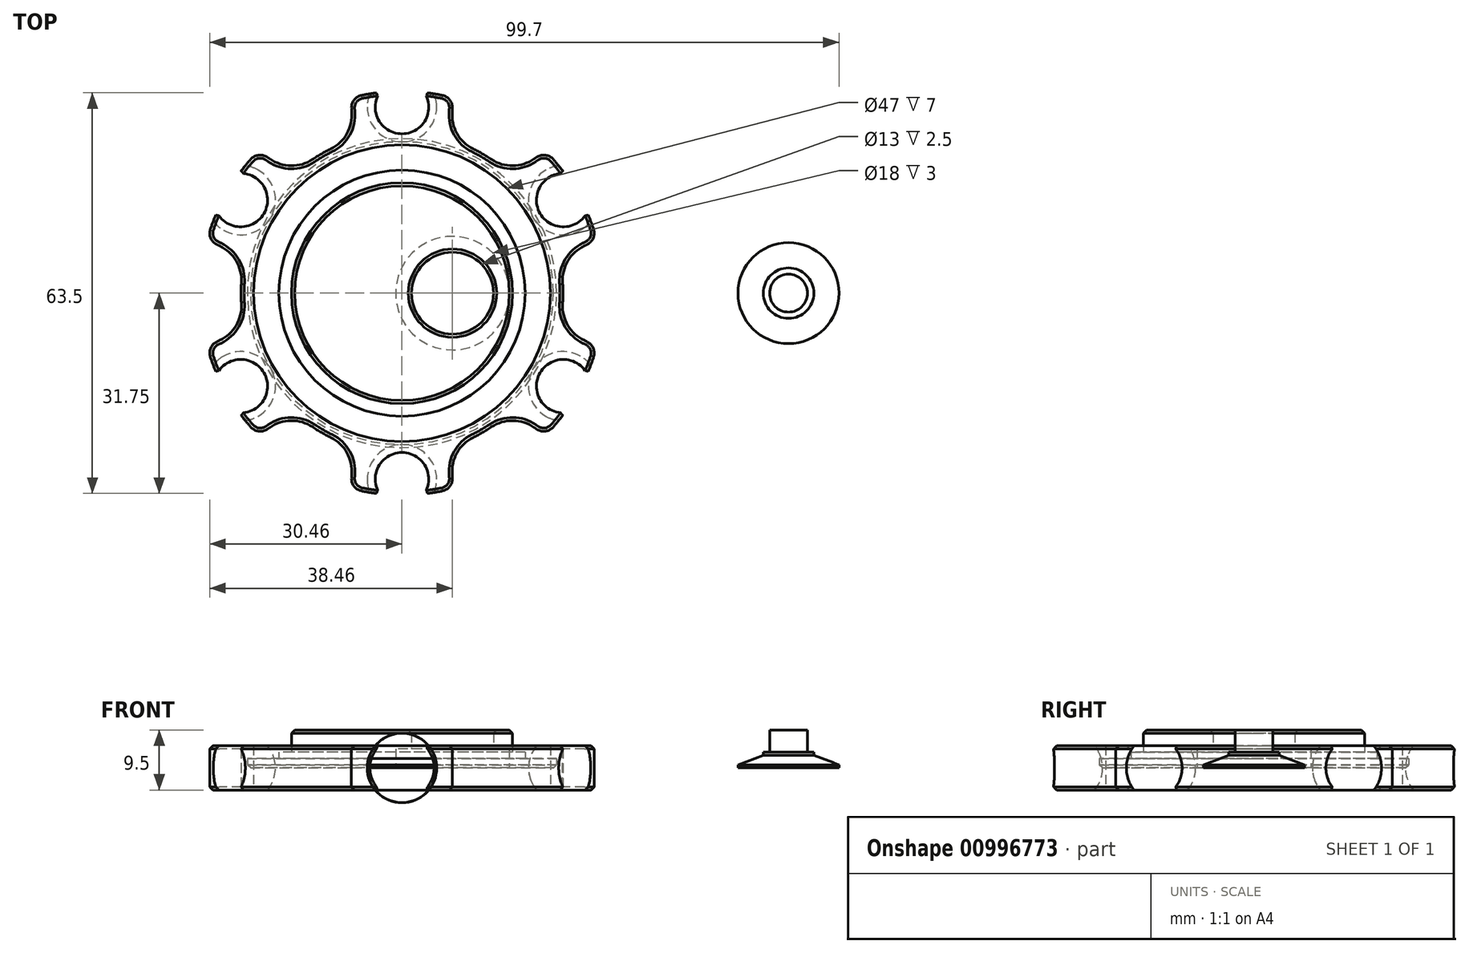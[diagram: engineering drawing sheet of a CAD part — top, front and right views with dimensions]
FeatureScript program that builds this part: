
annotation { "Feature Type Name" : "Feature", "Feature Type Description" : "" }
export const myFeature = defineFeature(function(context is Context, id is Id, definition is map)
    precondition{}
    {
        {
            var Q0;
            Q0=qCreatedBy(makeId("Top.planeOp"),FACE);
            var sketch = newSketch(context, id + "F0", { "sketchPlane" : qUnion([Q0])});
            skArc(sketch, "E0", {"start": v(-6.39, 24.69) * mm, "mid": v(0, -25.5) * mm, "end": v(6.39, 24.69) * mm});
            skArc(sketch, "E1", {"start": v(-2.55, 31.9) * mm, "mid": v(0, 26) * mm, "end": v(2.55, 31.9) * mm});
            skArc(sketch, "E2", {"start": v(7.85, 31.02) * mm, "mid": v(5.22, 31.57) * mm, "end": v(2.55, 31.9) * mm});
            skArc(sketch, "E3", {"start": v(-7.85, 31.02) * mm, "mid": v(-7.8, 27.7) * mm, "end": v(-6.39, 24.69) * mm});
            skArc(sketch, "E4.trimOffspring", {"start": v(6.39, 24.69) * mm, "mid": v(7.8, 27.7) * mm, "end": v(7.85, 31.02) * mm});
            skArc(sketch, "E5.trimOffspring", {"start": v(-2.55, 31.9) * mm, "mid": v(-5.22, 31.57) * mm, "end": v(-7.85, 31.02) * mm});
            skCircle(sketch, "E6", {"center": v(0, 0) * mm, "radius": 23.5 * mm});
            skSolve(sketch);
        }
        {
            var Q0;
            Q0=makeQuery(id+"F0.imprint","IMPRINT",FACE,{"disambiguationData":[TD([[makeQuery(id+"F0.imprint","IMPRINT",EDGE,{"derivedFrom":sQuery(id+"F0.wireOp",EDGE,"E0")}),1.0]])]});
            extrude(context, id + "F1", {"entities" : qUnion([Q0]), "depth" : 3.5 * mm, "offsetDistance" : 25 * mm, "hasSecondDirection" : true, "secondDirectionOppositeDirection" : true, "secondDirectionDepth" : 3.5 * mm});
        }
        {
            var Q0;
            Q0=makeQuery(id+"F1.opExtrude","SWEPT_EDGE",EDGE,{"disambiguationData":[OSD([sQuery(id+"F0.wireOp",EDGE,"E0"),sQuery(id+"F0.wireOp",EDGE,"E3")])]});
            var Q1;
            Q1=makeQuery(id+"F1.opExtrude","SWEPT_EDGE",EDGE,{"disambiguationData":[OSD([sQuery(id+"F0.wireOp",EDGE,"E0"),sQuery(id+"F0.wireOp",EDGE,"E4.trimOffspring")])]});
            fillet(context, id + "F2", {"entities" : qUnion([Q0, Q1]), "radius" : 6 * mm, "tangentPropagation" : true, "allowEdgeOverflow" : false});
        }
        {
            var Q0;
            Q0=makeQuery(id+"F1.opExtrude","SWEPT_EDGE",EDGE,{"disambiguationData":[OSD([sQuery(id+"F0.wireOp",EDGE,"E3"),sQuery(id+"F0.wireOp",EDGE,"E5.trimOffspring")])]});
            var Q1;
            Q1=makeQuery(id+"F1.opExtrude","SWEPT_EDGE",EDGE,{"disambiguationData":[OSD([sQuery(id+"F0.wireOp",EDGE,"E2"),sQuery(id+"F0.wireOp",EDGE,"E4.trimOffspring")])]});
            fillet(context, id + "F3", {"entities" : qUnion([Q0, Q1]), "radius" : 2 * mm, "tangentPropagation" : true, "allowEdgeOverflow" : false});
        }
        {
            var Q0;
            Q0=makeQuery(id+"F7.boolean.opBoolean","INTERSECT",EDGE,{"derivedFrom":[makeQuery(id+"F1.opExtrude","CAP_FACE",FACE,{"disambiguationData":[OSD([sQuery(id+"F0.wireOp",EDGE,"E0"),sQuery(id+"F0.wireOp",EDGE,"E1"),sQuery(id+"F0.wireOp",EDGE,"E2"),sQuery(id+"F0.wireOp",EDGE,"E3"),sQuery(id+"F0.wireOp",EDGE,"E4.trimOffspring"),sQuery(id+"F0.wireOp",EDGE,"E5.trimOffspring"),sQuery(id+"F0.wireOp",EDGE,"E6")])],"isStart":false}),makeQuery(id+"F7.opRevolve","SWEPT_FACE",FACE,{"disambiguationData":[OSD([sQuery(id+"F6.wireOp",EDGE,"E9")])]})]});
            var Q1;
            Q1=makeQuery(id+"F7.boolean.opBoolean","INTERSECT",EDGE,{"derivedFrom":[makeQuery(id+"F1.opExtrude","CAP_FACE",FACE,{"disambiguationData":[OSD([sQuery(id+"F0.wireOp",EDGE,"E0"),sQuery(id+"F0.wireOp",EDGE,"E1"),sQuery(id+"F0.wireOp",EDGE,"E2"),sQuery(id+"F0.wireOp",EDGE,"E3"),sQuery(id+"F0.wireOp",EDGE,"E4.trimOffspring"),sQuery(id+"F0.wireOp",EDGE,"E5.trimOffspring"),sQuery(id+"F0.wireOp",EDGE,"E6")])],"isStart":true}),makeQuery(id+"F7.opRevolve","SWEPT_FACE",FACE,{"disambiguationData":[OSD([sQuery(id+"F6.wireOp",EDGE,"E9")])]})]});
            var Q2;
            Q2=makeQuery(id+"F1.opExtrude","CAP_EDGE",EDGE,{"disambiguationData":[OSD([sQuery(id+"F0.wireOp",EDGE,"E5.trimOffspring")])],"isStart":true});
            var Q3;
            {var subQ0=sQuery(id+"F0.wireOp",EDGE,"E5.trimOffspring");var subQ1=sQuery(id+"F0.wireOp",EDGE,"E3");Q3=makeQuery(id+"F2.opFillet","BLEND_EDGE",EDGE,{"blendedFrom":[makeQuery(id+"F1.opExtrude","SWEPT_EDGE",EDGE,{"disambiguationData":[OSD([subQ1,subQ0])]}),makeQuery(id+"F1.opExtrude","CAP_FACE",FACE,{"disambiguationData":[OSD([sQuery(id+"F0.wireOp",EDGE,"E0"),sQuery(id+"F0.wireOp",EDGE,"E1"),sQuery(id+"F0.wireOp",EDGE,"E2"),subQ1,sQuery(id+"F0.wireOp",EDGE,"E4.trimOffspring"),subQ0,sQuery(id+"F0.wireOp",EDGE,"E6")])],"isStart":true})],"blendedInto":[makeQuery(id+"F1.opExtrude","CAP_FACE",FACE,{"disambiguationData":[OSD([sQuery(id+"F0.wireOp",EDGE,"E0"),sQuery(id+"F0.wireOp",EDGE,"E1"),sQuery(id+"F0.wireOp",EDGE,"E2"),subQ1,sQuery(id+"F0.wireOp",EDGE,"E4.trimOffspring"),subQ0,sQuery(id+"F0.wireOp",EDGE,"E6")])],"isStart":true})]});}
            var Q4;
            {var subQ0=sQuery(id+"F0.wireOp",EDGE,"E3");var subQ1=sQuery(id+"F0.wireOp",EDGE,"E0");Q4=makeQuery(id+"F2.opFillet","BLEND_EDGE",EDGE,{"blendedFrom":[makeQuery(id+"F1.opExtrude","SWEPT_EDGE",EDGE,{"disambiguationData":[OSD([subQ1,subQ0])]}),makeQuery(id+"F1.opExtrude","CAP_FACE",FACE,{"disambiguationData":[OSD([subQ1,sQuery(id+"F0.wireOp",EDGE,"E1"),sQuery(id+"F0.wireOp",EDGE,"E2"),subQ0,sQuery(id+"F0.wireOp",EDGE,"E4.trimOffspring"),sQuery(id+"F0.wireOp",EDGE,"E5.trimOffspring"),sQuery(id+"F0.wireOp",EDGE,"E6")])],"isStart":true})],"blendedInto":[makeQuery(id+"F1.opExtrude","CAP_FACE",FACE,{"disambiguationData":[OSD([subQ1,sQuery(id+"F0.wireOp",EDGE,"E1"),sQuery(id+"F0.wireOp",EDGE,"E2"),subQ0,sQuery(id+"F0.wireOp",EDGE,"E4.trimOffspring"),sQuery(id+"F0.wireOp",EDGE,"E5.trimOffspring"),sQuery(id+"F0.wireOp",EDGE,"E6")])],"isStart":true})]});}
            var Q5;
            Q5=makeQuery(id+"F1.opExtrude","CAP_EDGE",EDGE,{"disambiguationData":[OSD([sQuery(id+"F0.wireOp",EDGE,"E2")])],"isStart":false});
            var Q6;
            {var subQ0=sQuery(id+"F0.wireOp",EDGE,"E4.trimOffspring");var subQ1=sQuery(id+"F0.wireOp",EDGE,"E2");Q6=makeQuery(id+"F2.opFillet","BLEND_EDGE",EDGE,{"blendedFrom":[makeQuery(id+"F1.opExtrude","SWEPT_EDGE",EDGE,{"disambiguationData":[OSD([subQ1,subQ0])]}),makeQuery(id+"F1.opExtrude","CAP_FACE",FACE,{"disambiguationData":[OSD([sQuery(id+"F0.wireOp",EDGE,"E0"),sQuery(id+"F0.wireOp",EDGE,"E1"),subQ1,sQuery(id+"F0.wireOp",EDGE,"E3"),subQ0,sQuery(id+"F0.wireOp",EDGE,"E5.trimOffspring"),sQuery(id+"F0.wireOp",EDGE,"E6")])],"isStart":false})],"blendedInto":[makeQuery(id+"F1.opExtrude","CAP_FACE",FACE,{"disambiguationData":[OSD([sQuery(id+"F0.wireOp",EDGE,"E0"),sQuery(id+"F0.wireOp",EDGE,"E1"),subQ1,sQuery(id+"F0.wireOp",EDGE,"E3"),subQ0,sQuery(id+"F0.wireOp",EDGE,"E5.trimOffspring"),sQuery(id+"F0.wireOp",EDGE,"E6")])],"isStart":false})]});}
            var Q7;
            Q7=makeQuery(id+"F7.boolean.opBoolean","INTERSECT",EDGE,{"derivedFrom":[makeQuery(id+"F1.opExtrude","SWEPT_FACE",FACE,{"disambiguationData":[OSD([sQuery(id+"F0.wireOp",EDGE,"E5.trimOffspring")])]}),makeQuery(id+"F7.opRevolve","SWEPT_FACE",FACE,{"disambiguationData":[OSD([sQuery(id+"F6.wireOp",EDGE,"E9")])]})]});
            var Q8;
            Q8=makeQuery(id+"F7.boolean.opBoolean","INTERSECT",EDGE,{"derivedFrom":[makeQuery(id+"F1.opExtrude","SWEPT_FACE",FACE,{"disambiguationData":[OSD([sQuery(id+"F0.wireOp",EDGE,"E2")])]}),makeQuery(id+"F7.opRevolve","SWEPT_FACE",FACE,{"disambiguationData":[OSD([sQuery(id+"F6.wireOp",EDGE,"E9")])]})]});
            chamfer(context, id + "F4", {"entities" : qUnion([Q0, Q1, Q2, Q3, Q4, Q5, Q6, Q7, Q8]), "width" : 0.5 * mm, "tangentPropagation" : true});
        }
        {
            var Q0;
            Q0=makeQuery(id+"F1.opExtrude","SWEPT_BODY",BODY,{"disambiguationData":[OSD([sQuery(id+"F0.wireOp",EDGE,"E0"),sQuery(id+"F0.wireOp",EDGE,"E1"),sQuery(id+"F0.wireOp",EDGE,"E2"),sQuery(id+"F0.wireOp",EDGE,"E3"),sQuery(id+"F0.wireOp",EDGE,"E4.trimOffspring"),sQuery(id+"F0.wireOp",EDGE,"E5.trimOffspring"),sQuery(id+"F0.wireOp",EDGE,"E6")])]});
            var Q1;
            Q1=sQuery(id+"F0.wireOp",EDGE,"E6");
            var Q2;
            Q2=makeQuery(id+"F1.opExtrude","SWEPT_BODY",BODY,{"disambiguationData":[OSD([sQuery(id+"F0.wireOp",EDGE,"E0"),sQuery(id+"F0.wireOp",EDGE,"E1"),sQuery(id+"F0.wireOp",EDGE,"E2"),sQuery(id+"F0.wireOp",EDGE,"E3"),sQuery(id+"F0.wireOp",EDGE,"E4.trimOffspring"),sQuery(id+"F0.wireOp",EDGE,"E5.trimOffspring"),sQuery(id+"F0.wireOp",EDGE,"E6")])]});
            circularPattern(context, id + "F5", {"operationType" : NewBodyOperationType.ADD, "entities" : qUnion([Q0]), "axis" : qUnion([Q1]), "angle" : 360 * degree, "instanceCount" : 6, "equalSpace" : true});
        }
        {
            var Q0;
            Q0=qCreatedBy(makeId("Top.planeOp"),FACE);
            var sketch = newSketch(context, id + "F6", { "sketchPlane" : qUnion([Q0])});
            skLineSegment(sketch, "E7", {"start": v(-5.5, 29.5) * mm, "end": v(5.5, 29.5) * mm});
            skPoint(sketch, "E8.orphan", {"position": v(0, 29.5) * mm});
            skArc(sketch, "E9", {"start": v(-5.5, 29.5) * mm, "mid": v(0, 24) * mm, "end": v(5.5, 29.5) * mm});
            skLineSegment(sketch, "E10.1.0", {"start": v(-28.3, 9.99) * mm, "end": v(-22.8, 19.51) * mm});
            skArc(sketch, "E10.1.1", {"start": v(-28.3, 9.99) * mm, "mid": v(-20.78, 12) * mm, "end": v(-22.8, 19.51) * mm});
            skLineSegment(sketch, "E10.2.0", {"start": v(-22.8, -19.51) * mm, "end": v(-28.3, -9.99) * mm});
            skArc(sketch, "E10.2.1", {"start": v(-22.8, -19.51) * mm, "mid": v(-20.78, -12) * mm, "end": v(-28.3, -9.99) * mm});
            skLineSegment(sketch, "E10.3.0", {"start": v(5.5, -29.5) * mm, "end": v(-5.5, -29.5) * mm});
            skArc(sketch, "E10.3.1", {"start": v(5.5, -29.5) * mm, "mid": v(0, -24) * mm, "end": v(-5.5, -29.5) * mm});
            skLineSegment(sketch, "E10.4.0", {"start": v(28.3, -9.99) * mm, "end": v(22.8, -19.51) * mm});
            skArc(sketch, "E10.4.1", {"start": v(28.3, -9.99) * mm, "mid": v(20.78, -12) * mm, "end": v(22.8, -19.51) * mm});
            skLineSegment(sketch, "E10.5.0", {"start": v(22.8, 19.51) * mm, "end": v(28.3, 9.99) * mm});
            skArc(sketch, "E10.5.1", {"start": v(22.8, 19.51) * mm, "mid": v(20.78, 12) * mm, "end": v(28.3, 9.99) * mm});
            skPoint(sketch, "E10.center", {"position": v(0, 0) * mm});
            skSolve(sketch);
        }
        {
            var Q0;
            Q0=makeQuery(id+"F6.imprint","IMPRINT",FACE,{"disambiguationData":[TD([[makeQuery(id+"F6.imprint","IMPRINT",EDGE,{"derivedFrom":sQuery(id+"F6.wireOp",EDGE,"E7")}),-1.0]])]});
            var Q1;
            Q1=sQuery(id+"F6.wireOp",EDGE,"E7");
            revolve(context, id + "F7", {"operationType" : NewBodyOperationType.REMOVE, "surfaceOperationType" : NewSurfaceOperationType.NEW, "entities" : qUnion([Q0]), "axis" : qUnion([Q1]), "revolveType" : RevolveType.FULL, "oppositeDirection" : true});
        }
        {
            var Q0;
            Q0=makeQuery(id+"F6.imprint","IMPRINT",FACE,{"disambiguationData":[TD([[makeQuery(id+"F6.imprint","IMPRINT",EDGE,{"derivedFrom":sQuery(id+"F6.wireOp",EDGE,"E10.1.0")}),-1.0]])]});
            var Q1;
            Q1=sQuery(id+"F6.wireOp",EDGE,"E10.1.0");
            revolve(context, id + "F8", {"operationType" : NewBodyOperationType.REMOVE, "surfaceOperationType" : NewSurfaceOperationType.NEW, "entities" : qUnion([Q0]), "axis" : qUnion([Q1]), "revolveType" : RevolveType.FULL, "oppositeDirection" : true});
        }
        {
            var Q0;
            Q0=makeQuery(id+"F6.imprint","IMPRINT",FACE,{"disambiguationData":[TD([[makeQuery(id+"F6.imprint","IMPRINT",EDGE,{"derivedFrom":sQuery(id+"F6.wireOp",EDGE,"E10.2.0")}),-1.0]])]});
            var Q1;
            Q1=sQuery(id+"F6.wireOp",EDGE,"E10.2.0");
            revolve(context, id + "F9", {"operationType" : NewBodyOperationType.REMOVE, "surfaceOperationType" : NewSurfaceOperationType.NEW, "entities" : qUnion([Q0]), "axis" : qUnion([Q1]), "revolveType" : RevolveType.FULL, "oppositeDirection" : true});
        }
        {
            var Q0;
            Q0=makeQuery(id+"F6.imprint","IMPRINT",FACE,{"disambiguationData":[TD([[makeQuery(id+"F6.imprint","IMPRINT",EDGE,{"derivedFrom":sQuery(id+"F6.wireOp",EDGE,"E10.3.0")}),-1.0]])]});
            var Q1;
            Q1=sQuery(id+"F6.wireOp",EDGE,"E10.3.0");
            revolve(context, id + "F10", {"operationType" : NewBodyOperationType.REMOVE, "surfaceOperationType" : NewSurfaceOperationType.NEW, "entities" : qUnion([Q0]), "axis" : qUnion([Q1]), "revolveType" : RevolveType.FULL, "oppositeDirection" : true});
        }
        {
            var Q0;
            Q0=makeQuery(id+"F6.imprint","IMPRINT",FACE,{"disambiguationData":[TD([[makeQuery(id+"F6.imprint","IMPRINT",EDGE,{"derivedFrom":sQuery(id+"F6.wireOp",EDGE,"E10.4.0")}),-1.0]])]});
            var Q1;
            Q1=sQuery(id+"F6.wireOp",EDGE,"E10.4.0");
            revolve(context, id + "F11", {"operationType" : NewBodyOperationType.REMOVE, "surfaceOperationType" : NewSurfaceOperationType.NEW, "entities" : qUnion([Q0]), "axis" : qUnion([Q1]), "revolveType" : RevolveType.FULL, "oppositeDirection" : true});
        }
        {
            var Q0;
            Q0=makeQuery(id+"F6.imprint","IMPRINT",FACE,{"disambiguationData":[TD([[makeQuery(id+"F6.imprint","IMPRINT",EDGE,{"derivedFrom":sQuery(id+"F6.wireOp",EDGE,"E10.5.0")}),-1.0]])]});
            var Q1;
            Q1=sQuery(id+"F6.wireOp",EDGE,"E10.5.0");
            revolve(context, id + "F12", {"operationType" : NewBodyOperationType.REMOVE, "surfaceOperationType" : NewSurfaceOperationType.NEW, "entities" : qUnion([Q0]), "axis" : qUnion([Q1]), "revolveType" : RevolveType.FULL, "oppositeDirection" : true});
        }
        {
            var Q0;
            Q0=qCreatedBy(makeId("Top.planeOp"),FACE);
            var sketch = newSketch(context, id + "F13", { "sketchPlane" : qUnion([Q0])});
            skCircle(sketch, "E11", {"center": v(0, 0) * mm, "radius": 24.5 * mm});
            skCircle(sketch, "E12", {"center": v(0, 0) * mm, "radius": 17.5 * mm});
            skCircle(sketch, "E13", {"center": v(8, 0) * mm, "radius": 6.5 * mm});
            skCircle(sketch, "E14", {"center": v(0, 0) * mm, "radius": 19.5 * mm});
            skCircle(sketch, "E15", {"center": v(8, 0) * mm, "radius": 9 * mm});
            skSolve(sketch);
        }
        {
            var Q0;
            Q0=makeQuery(id+"F13.imprint","IMPRINT",FACE,{"disambiguationData":[TD([[makeQuery(id+"F13.imprint","IMPRINT",EDGE,{"derivedFrom":sQuery(id+"F13.wireOp",EDGE,"E11")}),1.0]])]});
            extrude(context, id + "F14", {"entities" : qUnion([Q0]), "depth" : 1.5 * mm, "offsetDistance" : 25 * mm});
        }
        {
            var Q0;
            Q0=makeQuery(id+"F13.imprint","IMPRINT",FACE,{"disambiguationData":[TD([[makeQuery(id+"F13.imprint","IMPRINT",EDGE,{"derivedFrom":sQuery(id+"F13.wireOp",EDGE,"E12")}),-1.0]])]});
            extrude(context, id + "F15", {"entities" : qUnion([Q0]), "operationType" : NewBodyOperationType.ADD, "depth" : 2.5 * mm, "offsetDistance" : 25 * mm});
        }
        {
            var Q0;
            Q0=makeQuery(id+"F13.imprint","IMPRINT",FACE,{"disambiguationData":[TD([[makeQuery(id+"F13.imprint","IMPRINT",EDGE,{"derivedFrom":sQuery(id+"F13.wireOp",EDGE,"E12")}),1.0]])]});
            var Q1;
            Q1=makeQuery(id+"F13.imprint","IMPRINT",FACE,{"disambiguationData":[TD([[makeQuery(id+"F13.imprint","IMPRINT",EDGE,{"derivedFrom":sQuery(id+"F13.wireOp",EDGE,"E13")}),-1.0]])]});
            extrude(context, id + "F16", {"entities" : qUnion([Q0, Q1]), "operationType" : NewBodyOperationType.ADD, "depth" : 6 * mm, "offsetDistance" : 25 * mm});
        }
        {
            var Q0;
            Q0=makeQuery(id+"F13.imprint","IMPRINT",FACE,{"disambiguationData":[TD([[makeQuery(id+"F13.imprint","IMPRINT",EDGE,{"derivedFrom":sQuery(id+"F13.wireOp",EDGE,"E13")}),-1.0]])]});
            extrude(context, id + "F17", {"entities" : qUnion([Q0]), "operationType" : NewBodyOperationType.REMOVE, "depth" : 3 * mm, "offsetDistance" : 25 * mm});
        }
        {
            var Q0;
            Q0=makeQuery(id+"F16.opExtrude","CAP_FACE",FACE,{"disambiguationData":[OSD([sQuery(id+"F13.wireOp",EDGE,"E12"),sQuery(id+"F13.wireOp",EDGE,"E13")])],"isStart":false});
            var Q1;
            Q1=makeQuery(id+"F14.opExtrude","CAP_EDGE",EDGE,{"disambiguationData":[OSD([sQuery(id+"F13.wireOp",EDGE,"E11")])],"isStart":true});
            chamfer(context, id + "F18", {"entities" : qUnion([Q0, Q1]), "width" : 0.5 * mm, "tangentPropagation" : true});
        }
        {
            var Q0;
            Q0=qCreatedBy(makeId("Front.planeOp"),FACE);
            var sketch = newSketch(context, id + "F19", { "sketchPlane" : qUnion([Q0])});
            skLineSegment(sketch, "E16", {"start": v(61.24, 6) * mm, "end": v(61.24, 0) * mm});
            skLineSegment(sketch, "E17", {"start": v(61.24, 0) * mm, "end": v(53.24, 0) * mm});
            skLineSegment(sketch, "E18", {"start": v(53.24, 0) * mm, "end": v(53.24, 0.5) * mm});
            skLineSegment(sketch, "E19", {"start": v(57.24, 2) * mm, "end": v(57.24, 2.5) * mm});
            skLineSegment(sketch, "E20", {"start": v(57.24, 2.5) * mm, "end": v(58.24, 2.5) * mm});
            skLineSegment(sketch, "E21", {"start": v(58.24, 2.5) * mm, "end": v(58.24, 6) * mm});
            skLineSegment(sketch, "E22", {"start": v(58.24, 6) * mm, "end": v(61.24, 6) * mm});
            skLineSegment(sketch, "E23", {"start": v(53.24, 0.5) * mm, "end": v(57.24, 2) * mm});
            skSolve(sketch);
        }
        {
            var Q0;
            Q0=makeQuery(id+"F19.imprint","IMPRINT",FACE,{"disambiguationData":[TD([[makeQuery(id+"F19.imprint","IMPRINT",EDGE,{"derivedFrom":sQuery(id+"F19.wireOp",EDGE,"E16")}),-1.0]])]});
            var Q1;
            Q1=sQuery(id+"F19.wireOp",EDGE,"E16");
            revolve(context, id + "F20", {"surfaceOperationType" : NewSurfaceOperationType.NEW, "entities" : qUnion([Q0]), "axis" : qUnion([Q1]), "revolveType" : RevolveType.FULL});
        }
    });
